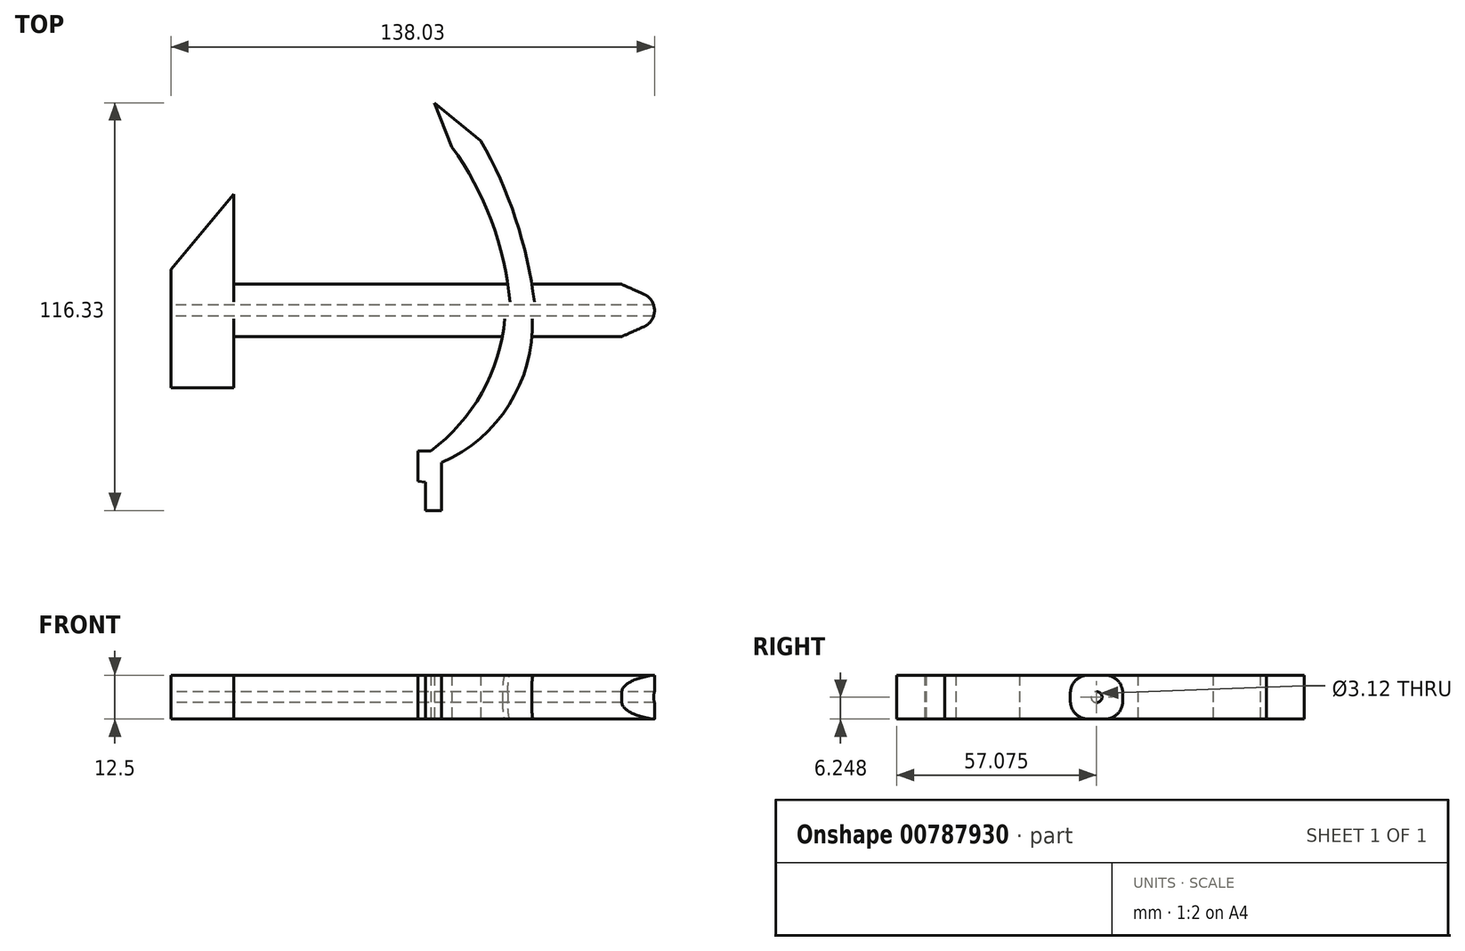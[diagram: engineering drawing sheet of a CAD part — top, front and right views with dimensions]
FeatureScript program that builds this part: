
annotation { "Feature Type Name" : "Feature", "Feature Type Description" : "" }
export const myFeature = defineFeature(function(context is Context, id is Id, definition is map)
    precondition{}
    {
        {
            var Q0;
            Q0=qCreatedBy(makeId("Top.planeOp"),FACE);
            var sketch = newSketch(context, id + "F0", { "sketchPlane" : qUnion([Q0])});
            skLineSegment(sketch, "E0", {"start": v(-8.92, 0) * mm, "end": v(-93.98, 0) * mm});
            skLineSegment(sketch, "E1", {"start": v(-93.98, 0) * mm, "end": v(-93.98, -14.57) * mm});
            skLineSegment(sketch, "E2", {"start": v(-93.98, -14.57) * mm, "end": v(-111.92, -14.57) * mm});
            skLineSegment(sketch, "E3", {"start": v(-111.92, -14.57) * mm, "end": v(-111.92, 14.57) * mm});
            skLineSegment(sketch, "E4", {"start": v(-93.98, 14.97) * mm, "end": v(-93.98, 0) * mm});
            skLineSegment(sketch, "E5", {"start": v(-93.98, 14.97) * mm, "end": v(-8.92, 14.97) * mm});
            skPoint(sketch, "E6.end.orphan", {"position": v(-93.98, 29.94) * mm});
            skLineSegment(sketch, "E7", {"start": v(-111.92, 14.57) * mm, "end": v(-111.92, 19.22) * mm});
            skLineSegment(sketch, "E8", {"start": v(-111.92, 19.22) * mm, "end": v(-93.98, 40.68) * mm});
            skLineSegment(sketch, "E9", {"start": v(-93.98, 40.68) * mm, "end": v(-93.98, 14.97) * mm});
            skArc(sketch, "E10", {"start": v(-37.75, -32.62) * mm, "mid": v(-24.46, -18.23) * mm, "end": v(-17.32, 0) * mm});
            skArc(sketch, "E11", {"start": v(-34.68, -35.91) * mm, "mid": v(-16.81, -21.53) * mm, "end": v(-8.92, 0) * mm});
            skLineSegment(sketch, "E12", {"start": v(-37.75, -32.62) * mm, "end": v(-41.4, -32.62) * mm});
            skLineSegment(sketch, "E13", {"start": v(-41.4, -32.62) * mm, "end": v(-41.4, -41.25) * mm});
            skLineSegment(sketch, "E14", {"start": v(-41.4, -41.25) * mm, "end": v(-39.21, -41.55) * mm});
            skLineSegment(sketch, "E15", {"start": v(-39.21, -41.55) * mm, "end": v(-39.21, -49.6) * mm});
            skLineSegment(sketch, "E16", {"start": v(-39.21, -49.6) * mm, "end": v(-34.68, -49.6) * mm});
            skLineSegment(sketch, "E17", {"start": v(-34.68, -49.6) * mm, "end": v(-34.68, -35.91) * mm});
            skPoint(sketch, "E18.end.orphan", {"position": v(-17.32, 14.97) * mm});
            skPoint(sketch, "E19.end.orphan", {"position": v(-8.92, 14.97) * mm});
            skArc(sketch, "E20", {"start": v(-17.32, 0) * mm, "mid": v(-16.2, 7.45) * mm, "end": v(-15.77, 14.97) * mm});
            skArc(sketch, "E21", {"start": v(-8.92, 0) * mm, "mid": v(-8.05, 7.49) * mm, "end": v(-8.92, 14.97) * mm});
            skArc(sketch, "E22", {"start": v(-15.77, 14.97) * mm, "mid": v(-21.38, 35.52) * mm, "end": v(-31.73, 54.14) * mm});
            skArc(sketch, "E23", {"start": v(-8.92, 14.97) * mm, "mid": v(-14.38, 36.1) * mm, "end": v(-23.5, 55.94) * mm});
            skLineSegment(sketch, "E24", {"start": v(-23.5, 55.94) * mm, "end": v(-36.68, 66.74) * mm});
            skLineSegment(sketch, "E25", {"start": v(-36.68, 66.74) * mm, "end": v(-31.73, 54.14) * mm});
            skPoint(sketch, "E26.start.orphan", {"position": v(54.28, 0) * mm});
            skPoint(sketch, "E27.orphan", {"position": v(0, 14.97) * mm});
            skLineSegment(sketch, "E28", {"start": v(-8.92, 14.97) * mm, "end": v(16.7, 14.97) * mm});
            skLineSegment(sketch, "E29", {"start": v(16.7, 14.97) * mm, "end": v(16.7, 0) * mm});
            skLineSegment(sketch, "E30", {"start": v(16.7, 0) * mm, "end": v(-8.92, 0) * mm});
            skLineSegment(sketch, "E31", {"start": v(-93.98, 7.49) * mm, "end": v(16.7, 7.49) * mm});
            skLineSegment(sketch, "E32", {"start": v(16.7, 14.97) * mm, "end": v(33.53, 7.49) * mm});
            skLineSegment(sketch, "E33", {"start": v(33.53, 7.49) * mm, "end": v(16.7, 0) * mm});
            skSolve(sketch);
        }
        {
            var Q0;
            {var subQ0=sQuery(id+"F0.wireOp",EDGE,"E4");Q0=makeQuery(id+"F0.imprint","IMPRINT",FACE,{"disambiguationData":[TD([[makeQuery(id+"F0.imprint","IMPRINT",EDGE,{"derivedFrom":subQ0}),1.0]])]});}
            var Q1;
            {var subQ0=sQuery(id+"F0.wireOp",EDGE,"JpQOhbZm-w84l-KoDQ-Hadm-NlJd4A4tbMOI");Q1=makeQuery(id+"F0.imprint","IMPRINT",FACE,{"disambiguationData":[TD([[makeQuery(id+"F0.imprint","IMPRINT",EDGE,{"derivedFrom":subQ0}),-1.0]])]});}
            var Q2;
            {var subQ0=sQuery(id+"F0.wireOp",EDGE,"E19");Q2=makeQuery(id+"F0.imprint","IMPRINT",FACE,{"disambiguationData":[TD([[makeQuery(id+"F0.imprint","IMPRINT",EDGE,{"derivedFrom":subQ0}),-1.0]])]});}
            var Q3;
            Q3=makeQuery(id+"F0.imprint","IMPRINT",FACE,{"disambiguationData":[TD([[makeQuery(id+"F0.imprint","IMPRINT",EDGE,{"derivedFrom":sQuery(id+"F0.wireOp",EDGE,"fDL4QrL3-Pscx-cP9W-Lwa4-rLpFBMJqSzpK")}),-1.0]])]});
            var Q4;
            {var subQ3=sQuery(id+"F0.wireOp",EDGE,"7gnIvbm1-Tzpb-HQnP-gJyo-X1fORrnEBfei");Q4=makeQuery(id+"F0.imprint","IMPRINT",FACE,{"disambiguationData":[TD([[makeQuery(id+"F0.imprint","IMPRINT",EDGE,{"derivedFrom":subQ3}),-1.0]])]});}
            var Q5;
            Q5=makeQuery(id+"F0.imprint","IMPRINT",FACE,{"disambiguationData":[TD([[makeQuery(id+"F0.imprint","IMPRINT",EDGE,{"derivedFrom":sQuery(id+"F0.wireOp",EDGE,"QAosD0dB-YqBm-HPNd-WOXU-6VFVhD7WSS9p")}),1.0]])]});
            var Q6;
            Q6=makeQuery(id+"F0.imprint","IMPRINT",FACE,{"disambiguationData":[TD([[makeQuery(id+"F0.imprint","IMPRINT",EDGE,{"derivedFrom":sQuery(id+"F0.wireOp",EDGE,"E1")}),-1.0]])]});
            var Q7;
            {var subQ0=sQuery(id+"F0.wireOp",EDGE,"E22");Q7=makeQuery(id+"F0.imprint","IMPRINT",FACE,{"disambiguationData":[TD([[makeQuery(id+"F0.imprint","IMPRINT",EDGE,{"derivedFrom":subQ0}),-1.0]])]});}
            var Q8;
            {var subQ0=sQuery(id+"F0.wireOp",EDGE,"E20");Q8=makeQuery(id+"F0.imprint","IMPRINT",FACE,{"disambiguationData":[TD([[makeQuery(id+"F0.imprint","IMPRINT",EDGE,{"derivedFrom":subQ0}),-1.0]])]});}
            var Q9;
            {var subQ1=sQuery(id+"F0.wireOp",EDGE,"E10");Q9=makeQuery(id+"F0.imprint","IMPRINT",FACE,{"disambiguationData":[TD([[makeQuery(id+"F0.imprint","IMPRINT",EDGE,{"derivedFrom":subQ1}),-1.0]])]});}
            var Q10;
            {var subQ0=sQuery(id+"F0.wireOp",EDGE,"E28");Q10=makeQuery(id+"F0.imprint","IMPRINT",FACE,{"disambiguationData":[TD([[makeQuery(id+"F0.imprint","IMPRINT",EDGE,{"derivedFrom":subQ0}),-1.0]])]});}
            var Q11;
            {var subQ0=sQuery(id+"F0.wireOp",EDGE,"E30");Q11=makeQuery(id+"F0.imprint","IMPRINT",FACE,{"disambiguationData":[TD([[makeQuery(id+"F0.imprint","IMPRINT",EDGE,{"derivedFrom":subQ0}),-1.0]])]});}
            var Q12;
            {var subQ0=sQuery(id+"F0.wireOp",EDGE,"E32");Q12=makeQuery(id+"F0.imprint","IMPRINT",FACE,{"disambiguationData":[TD([[makeQuery(id+"F0.imprint","IMPRINT",EDGE,{"derivedFrom":subQ0}),-1.0]])]});}
            extrude(context, id + "F1", {"entities" : qUnion([Q0, Q1, Q2, Q3, Q4, Q5, Q6, Q7, Q8, Q9, Q10, Q11, Q12]), "depth" : 12.5 * mm, "offsetDistance" : 25.4 * mm});
        }
        {
            var Q0;
            Q0=makeQuery(id+"F1.opExtrude","SWEPT_FACE",FACE,{"disambiguationData":[OSD([sQuery(id+"F0.wireOp",EDGE,"E3"),sQuery(id+"F0.wireOp",EDGE,"E7")])]});
            var sketch = newSketch(context, id + "F2", { "sketchPlane" : qUnion([Q0])});
            skLineSegment(sketch, "E34.0", {"start": v(-7.49, 12.5) * mm, "end": v(-7.49, 0) * mm});
            skCircle(sketch, "E35", {"center": v(-7.49, 6.25) * mm, "radius": 1.56 * mm});
            skSolve(sketch);
        }
        {
            var Q0;
            Q0 = qSketchRegion(id + "F2", true);
            extrude(context, id + "F3", {"entities" : qUnion([Q0]), "operationType" : NewBodyOperationType.REMOVE, "oppositeDirection" : true, "depth" : 152.4 * mm, "offsetDistance" : 25.4 * mm});
        }
        {
            var Q0;
            {var subQ0=sQuery(id+"F0.wireOp",EDGE,"E33");var subQ1=sQuery(id+"F0.wireOp",EDGE,"E32");Q0=makeQuery(id+"F3.boolean.opBoolean","SPLIT",EDGE,{"disambiguationData":[TD([makeQuery(id+"F1.opExtrude","CAP_FACE",FACE,{"disambiguationData":[OSD([sQuery(id+"F0.wireOp",EDGE,"E0"),sQuery(id+"F0.wireOp",EDGE,"E1"),sQuery(id+"F0.wireOp",EDGE,"E2"),sQuery(id+"F0.wireOp",EDGE,"E3"),sQuery(id+"F0.wireOp",EDGE,"E5"),sQuery(id+"F0.wireOp",EDGE,"E7"),sQuery(id+"F0.wireOp",EDGE,"E8"),sQuery(id+"F0.wireOp",EDGE,"E9"),sQuery(id+"F0.wireOp",EDGE,"E10"),sQuery(id+"F0.wireOp",EDGE,"E11"),sQuery(id+"F0.wireOp",EDGE,"E12"),sQuery(id+"F0.wireOp",EDGE,"E13"),sQuery(id+"F0.wireOp",EDGE,"E14"),sQuery(id+"F0.wireOp",EDGE,"E15"),sQuery(id+"F0.wireOp",EDGE,"E16"),sQuery(id+"F0.wireOp",EDGE,"E17"),sQuery(id+"F0.wireOp",EDGE,"E22"),sQuery(id+"F0.wireOp",EDGE,"E23"),sQuery(id+"F0.wireOp",EDGE,"E24"),sQuery(id+"F0.wireOp",EDGE,"E25"),sQuery(id+"F0.wireOp",EDGE,"E28"),sQuery(id+"F0.wireOp",EDGE,"E30"),subQ1,subQ0])],"isStart":true})])],"derivedFrom":makeQuery(id+"F1.opExtrude","SWEPT_EDGE",EDGE,{"disambiguationData":[OSD([subQ1,subQ0])]})});}
            fillet(context, id + "F4", {"entities" : qUnion([Q0]), "radius" : 5.08 * mm, "tangentPropagation" : true, "allowEdgeOverflow" : false});
        }
        {
            var Q0;
            Q0=makeQuery(id+"F1.opExtrude","CAP_EDGE",EDGE,{"disambiguationData":[OSD([sQuery(id+"F0.wireOp",EDGE,"E30")])],"isStart":false});
            var Q1;
            Q1=makeQuery(id+"F1.opExtrude","CAP_EDGE",EDGE,{"disambiguationData":[OSD([sQuery(id+"F0.wireOp",EDGE,"E28")])],"isStart":false});
            var Q2;
            Q2=makeQuery(id+"F1.opExtrude","CAP_EDGE",EDGE,{"disambiguationData":[OSD([sQuery(id+"F0.wireOp",EDGE,"E30")])],"isStart":true});
            var Q3;
            Q3=makeQuery(id+"F1.opExtrude","CAP_EDGE",EDGE,{"disambiguationData":[OSD([sQuery(id+"F0.wireOp",EDGE,"E28")])],"isStart":true});
            var Q4;
            Q4=makeQuery(id+"F1.opExtrude","CAP_EDGE",EDGE,{"disambiguationData":[OSD([sQuery(id+"F0.wireOp",EDGE,"E5")])],"isStart":false});
            var Q5;
            Q5=makeQuery(id+"F1.opExtrude","CAP_EDGE",EDGE,{"disambiguationData":[OSD([sQuery(id+"F0.wireOp",EDGE,"E0")])],"isStart":false});
            var Q6;
            Q6=makeQuery(id+"F1.opExtrude","CAP_EDGE",EDGE,{"disambiguationData":[OSD([sQuery(id+"F0.wireOp",EDGE,"E0")])],"isStart":true});
            var Q7;
            Q7=makeQuery(id+"F1.opExtrude","CAP_EDGE",EDGE,{"disambiguationData":[OSD([sQuery(id+"F0.wireOp",EDGE,"E5")])],"isStart":true});
            fillet(context, id + "F5", {"entities" : qUnion([Q0, Q1, Q2, Q3, Q4, Q5, Q6, Q7]), "radius" : 5.08 * mm, "tangentPropagation" : true, "allowEdgeOverflow" : false});
        }
    });
